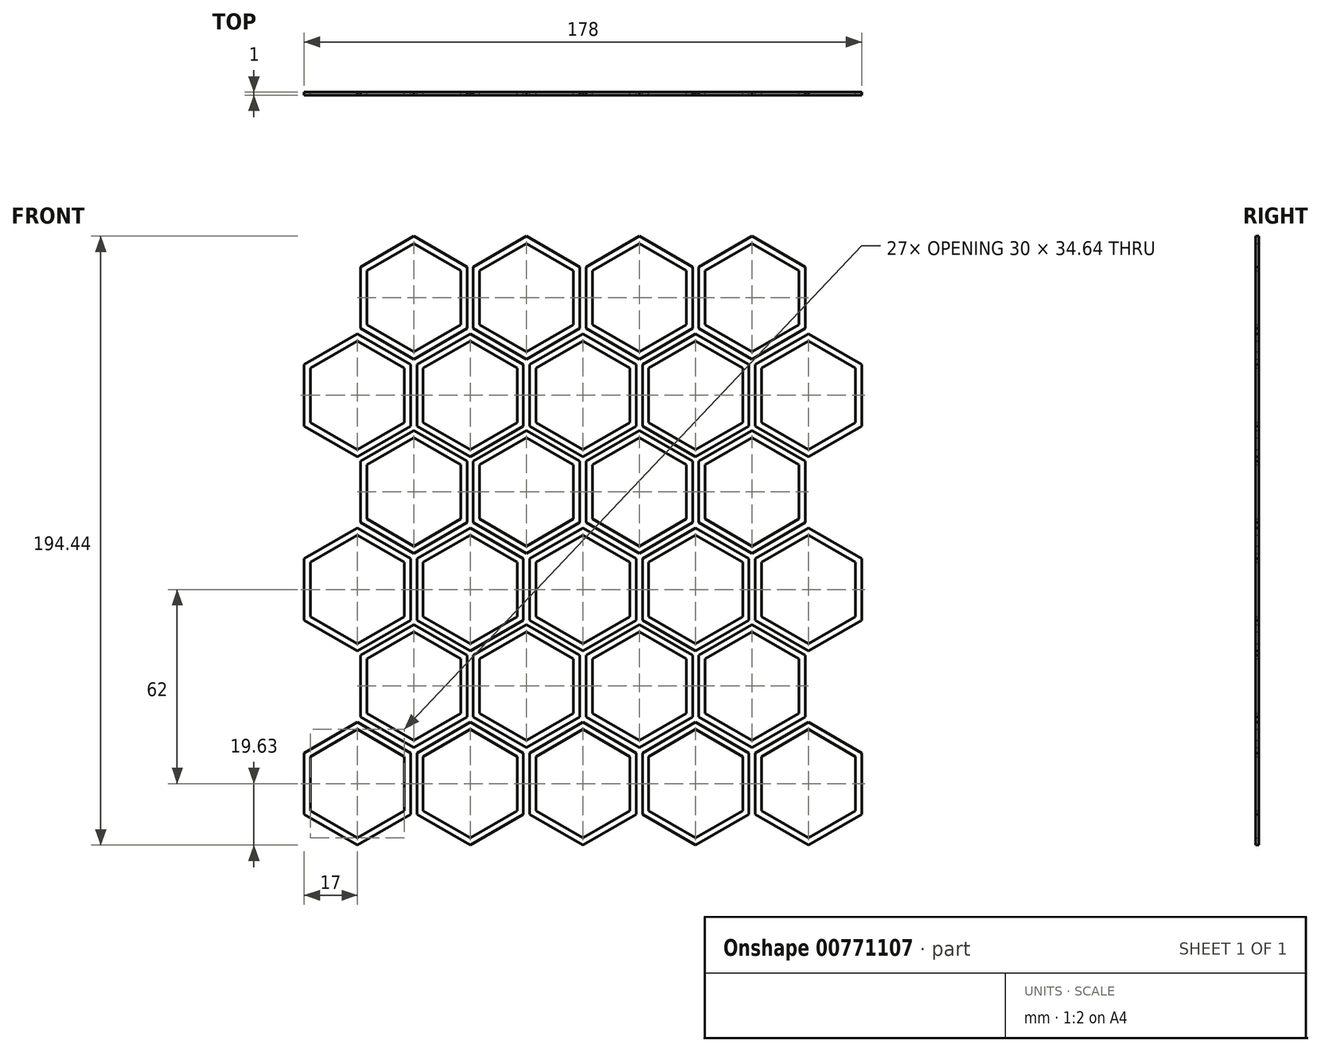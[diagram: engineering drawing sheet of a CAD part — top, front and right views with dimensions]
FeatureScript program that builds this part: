
annotation { "Feature Type Name" : "Feature", "Feature Type Description" : "" }
export const myFeature = defineFeature(function(context is Context, id is Id, definition is map)
    precondition{}
    {
        {
            var Q0;
            Q0=qCreatedBy(makeId("Front.planeOp"),FACE);
            var sketch = newSketch(context, id + "F0", { "sketchPlane" : qUnion([Q0])});
            skCircle(sketch, "E0.cCircle", {"center": v(0, 0) * mm, "radius": 15 * mm, "construction": true});
            skLineSegment(sketch, "E0.0", {"start": v(15, 8.66) * mm, "end": v(15, -8.66) * mm});
            skLineSegment(sketch, "E0.1", {"start": v(15, -8.66) * mm, "end": v(0, -17.32) * mm});
            skLineSegment(sketch, "E0.2", {"start": v(0, -17.32) * mm, "end": v(-15, -8.66) * mm});
            skLineSegment(sketch, "E0.3", {"start": v(-15, -8.66) * mm, "end": v(-15, 8.66) * mm});
            skLineSegment(sketch, "E0.4", {"start": v(-15, 8.66) * mm, "end": v(0, 17.32) * mm});
            skLineSegment(sketch, "E0.5", {"start": v(0, 17.32) * mm, "end": v(15, 8.66) * mm});
            skPoint(sketch, "E0.0.midPoint", {"position": v(15, 0) * mm});
            skLineSegment(sketch, "E1.0", {"start": v(0, 19.63) * mm, "end": v(17, 9.81) * mm});
            skLineSegment(sketch, "E1.1", {"start": v(17, -9.81) * mm, "end": v(0, -19.63) * mm});
            skLineSegment(sketch, "E1.2", {"start": v(0, -19.63) * mm, "end": v(-17, -9.81) * mm});
            skLineSegment(sketch, "E1.3", {"start": v(17, 9.81) * mm, "end": v(17, -9.81) * mm});
            skLineSegment(sketch, "E1.4", {"start": v(-17, -9.81) * mm, "end": v(-17, 9.81) * mm});
            skLineSegment(sketch, "E1.5", {"start": v(-17, 9.81) * mm, "end": v(0, 19.63) * mm});
            skLineSegment(sketch, "E2.1.0.0", {"start": v(36, 17.32) * mm, "end": v(51, 8.66) * mm});
            skLineSegment(sketch, "E2.1.0.1", {"start": v(36, 19.63) * mm, "end": v(53, 9.81) * mm});
            skLineSegment(sketch, "E2.1.0.2", {"start": v(53, -9.81) * mm, "end": v(36, -19.63) * mm});
            skLineSegment(sketch, "E2.1.0.3", {"start": v(36, -19.63) * mm, "end": v(19, -9.81) * mm});
            skLineSegment(sketch, "E2.1.0.4", {"start": v(53, 9.81) * mm, "end": v(53, -9.81) * mm});
            skLineSegment(sketch, "E2.1.0.5", {"start": v(19, -9.81) * mm, "end": v(19, 9.81) * mm});
            skLineSegment(sketch, "E2.1.0.6", {"start": v(19, 9.81) * mm, "end": v(36, 19.63) * mm});
            skPoint(sketch, "E2.1.0.7", {"position": v(51, 0) * mm});
            skLineSegment(sketch, "E2.1.0.8", {"start": v(21, 8.66) * mm, "end": v(36, 17.32) * mm});
            skLineSegment(sketch, "E2.1.0.9", {"start": v(21, -8.66) * mm, "end": v(21, 8.66) * mm});
            skLineSegment(sketch, "E2.1.0.10", {"start": v(36, -17.32) * mm, "end": v(21, -8.66) * mm});
            skLineSegment(sketch, "E2.1.0.11", {"start": v(51, -8.66) * mm, "end": v(36, -17.32) * mm});
            skLineSegment(sketch, "E2.1.0.12", {"start": v(51, 8.66) * mm, "end": v(51, -8.66) * mm});
            skCircle(sketch, "E2.1.0.13", {"center": v(36, 0) * mm, "radius": 15 * mm, "construction": true});
            skLineSegment(sketch, "E2.2.0.0", {"start": v(72, 17.32) * mm, "end": v(87, 8.66) * mm});
            skLineSegment(sketch, "E2.2.0.1", {"start": v(72, 19.63) * mm, "end": v(89, 9.81) * mm});
            skLineSegment(sketch, "E2.2.0.2", {"start": v(89, -9.81) * mm, "end": v(72, -19.63) * mm});
            skLineSegment(sketch, "E2.2.0.3", {"start": v(72, -19.63) * mm, "end": v(55, -9.81) * mm});
            skLineSegment(sketch, "E2.2.0.4", {"start": v(89, 9.81) * mm, "end": v(89, -9.81) * mm});
            skLineSegment(sketch, "E2.2.0.5", {"start": v(55, -9.81) * mm, "end": v(55, 9.81) * mm});
            skLineSegment(sketch, "E2.2.0.6", {"start": v(55, 9.81) * mm, "end": v(72, 19.63) * mm});
            skPoint(sketch, "E2.2.0.7", {"position": v(87, 0) * mm});
            skLineSegment(sketch, "E2.2.0.8", {"start": v(57, 8.66) * mm, "end": v(72, 17.32) * mm});
            skLineSegment(sketch, "E2.2.0.9", {"start": v(57, -8.66) * mm, "end": v(57, 8.66) * mm});
            skLineSegment(sketch, "E2.2.0.10", {"start": v(72, -17.32) * mm, "end": v(57, -8.66) * mm});
            skLineSegment(sketch, "E2.2.0.11", {"start": v(87, -8.66) * mm, "end": v(72, -17.32) * mm});
            skLineSegment(sketch, "E2.2.0.12", {"start": v(87, 8.66) * mm, "end": v(87, -8.66) * mm});
            skCircle(sketch, "E2.2.0.13", {"center": v(72, 0) * mm, "radius": 15 * mm, "construction": true});
            skLineSegment(sketch, "E2.direction1", {"start": v(-17, -9.81) * mm, "end": v(19, -9.81) * mm, "construction": true});
            skLineSegment(sketch, "E3", {"start": v(18, 6.46) * mm, "end": v(18, 61.1) * mm, "construction": true});
            skCircle(sketch, "E4.cCircle", {"center": v(18, 31.18) * mm, "radius": 15 * mm, "construction": true});
            skLineSegment(sketch, "E4.0", {"start": v(33, 39.84) * mm, "end": v(33, 22.52) * mm});
            skLineSegment(sketch, "E4.1", {"start": v(33, 22.52) * mm, "end": v(18, 13.86) * mm});
            skLineSegment(sketch, "E4.2", {"start": v(18, 13.86) * mm, "end": v(3, 22.52) * mm});
            skLineSegment(sketch, "E4.3", {"start": v(3, 22.52) * mm, "end": v(3, 39.84) * mm});
            skLineSegment(sketch, "E4.4", {"start": v(3, 39.84) * mm, "end": v(18, 48.5) * mm});
            skLineSegment(sketch, "E4.5", {"start": v(18, 48.5) * mm, "end": v(33, 39.84) * mm});
            skPoint(sketch, "E4.0.midPoint", {"position": v(33, 31.18) * mm});
            skLineSegment(sketch, "E5.1.0.0", {"start": v(54, 48.5) * mm, "end": v(69, 39.84) * mm});
            skLineSegment(sketch, "E5.1.0.1", {"start": v(39, 39.84) * mm, "end": v(54, 48.5) * mm});
            skLineSegment(sketch, "E5.1.0.2", {"start": v(39, 22.52) * mm, "end": v(39, 39.84) * mm});
            skLineSegment(sketch, "E5.1.0.3", {"start": v(54, 13.86) * mm, "end": v(39, 22.52) * mm});
            skLineSegment(sketch, "E5.1.0.4", {"start": v(69, 22.52) * mm, "end": v(54, 13.86) * mm});
            skLineSegment(sketch, "E5.1.0.5", {"start": v(69, 39.84) * mm, "end": v(69, 22.52) * mm});
            skLineSegment(sketch, "E5.direction1", {"start": v(3, 22.52) * mm, "end": v(39, 22.52) * mm, "construction": true});
            skLineSegment(sketch, "E6.0", {"start": v(35, 21.36) * mm, "end": v(18, 11.55) * mm});
            skLineSegment(sketch, "E6.1", {"start": v(1, 21.36) * mm, "end": v(1, 41) * mm});
            skLineSegment(sketch, "E6.2", {"start": v(1, 41) * mm, "end": v(18, 50.8) * mm});
            skLineSegment(sketch, "E6.3", {"start": v(18, 11.55) * mm, "end": v(1, 21.36) * mm});
            skLineSegment(sketch, "E6.4", {"start": v(18, 50.8) * mm, "end": v(35, 41) * mm});
            skLineSegment(sketch, "E6.5", {"start": v(35, 41) * mm, "end": v(35, 21.36) * mm});
            skLineSegment(sketch, "E7.0", {"start": v(37, 21.36) * mm, "end": v(37, 41) * mm});
            skLineSegment(sketch, "E7.1", {"start": v(54, 50.8) * mm, "end": v(71, 41) * mm});
            skLineSegment(sketch, "E7.2", {"start": v(71, 41) * mm, "end": v(71, 21.36) * mm});
            skLineSegment(sketch, "E7.3", {"start": v(37, 41) * mm, "end": v(54, 50.8) * mm});
            skLineSegment(sketch, "E7.4", {"start": v(71, 21.36) * mm, "end": v(54, 11.55) * mm});
            skLineSegment(sketch, "E7.5", {"start": v(54, 11.55) * mm, "end": v(37, 21.36) * mm});
            skLineSegment(sketch, "E8.0.3.0", {"start": v(108, 17.32) * mm, "end": v(123, 8.66) * mm});
            skLineSegment(sketch, "E8.3.3.0", {"start": v(108, 19.63) * mm, "end": v(125, 9.81) * mm});
            skLineSegment(sketch, "E8.6.3.0", {"start": v(125, -9.81) * mm, "end": v(108, -19.63) * mm});
            skLineSegment(sketch, "E8.9.3.0", {"start": v(108, -19.63) * mm, "end": v(91, -9.81) * mm});
            skLineSegment(sketch, "E8.12.3.0", {"start": v(125, 9.81) * mm, "end": v(125, -9.81) * mm});
            skLineSegment(sketch, "E8.15.3.0", {"start": v(91, -9.81) * mm, "end": v(91, 9.81) * mm});
            skLineSegment(sketch, "E8.18.3.0", {"start": v(91, 9.81) * mm, "end": v(108, 19.63) * mm});
            skPoint(sketch, "E8.21.3.0", {"position": v(123, 0) * mm});
            skLineSegment(sketch, "E8.22.3.0", {"start": v(93, 8.66) * mm, "end": v(108, 17.32) * mm});
            skLineSegment(sketch, "E8.25.3.0", {"start": v(93, -8.66) * mm, "end": v(93, 8.66) * mm});
            skLineSegment(sketch, "E8.28.3.0", {"start": v(108, -17.32) * mm, "end": v(93, -8.66) * mm});
            skLineSegment(sketch, "E8.31.3.0", {"start": v(123, -8.66) * mm, "end": v(108, -17.32) * mm});
            skLineSegment(sketch, "E8.34.3.0", {"start": v(123, 8.66) * mm, "end": v(123, -8.66) * mm});
            skCircle(sketch, "E8.37.3.0", {"center": v(108, 0) * mm, "radius": 15 * mm, "construction": true});
            skLineSegment(sketch, "E8.0.4.0", {"start": v(144, 17.32) * mm, "end": v(159, 8.66) * mm});
            skLineSegment(sketch, "E8.3.4.0", {"start": v(144, 19.63) * mm, "end": v(161, 9.81) * mm});
            skLineSegment(sketch, "E8.6.4.0", {"start": v(161, -9.81) * mm, "end": v(144, -19.63) * mm});
            skLineSegment(sketch, "E8.9.4.0", {"start": v(144, -19.63) * mm, "end": v(127, -9.81) * mm});
            skLineSegment(sketch, "E8.12.4.0", {"start": v(161, 9.81) * mm, "end": v(161, -9.81) * mm});
            skLineSegment(sketch, "E8.15.4.0", {"start": v(127, -9.81) * mm, "end": v(127, 9.81) * mm});
            skLineSegment(sketch, "E8.18.4.0", {"start": v(127, 9.81) * mm, "end": v(144, 19.63) * mm});
            skPoint(sketch, "E8.21.4.0", {"position": v(159, 0) * mm});
            skLineSegment(sketch, "E8.22.4.0", {"start": v(129, 8.66) * mm, "end": v(144, 17.32) * mm});
            skLineSegment(sketch, "E8.25.4.0", {"start": v(129, -8.66) * mm, "end": v(129, 8.66) * mm});
            skLineSegment(sketch, "E8.28.4.0", {"start": v(144, -17.32) * mm, "end": v(129, -8.66) * mm});
            skLineSegment(sketch, "E8.31.4.0", {"start": v(159, -8.66) * mm, "end": v(144, -17.32) * mm});
            skLineSegment(sketch, "E8.34.4.0", {"start": v(159, 8.66) * mm, "end": v(159, -8.66) * mm});
            skCircle(sketch, "E8.37.4.0", {"center": v(144, 0) * mm, "radius": 15 * mm, "construction": true});
            skLineSegment(sketch, "E9.0.2.0", {"start": v(90, 48.5) * mm, "end": v(105, 39.84) * mm});
            skLineSegment(sketch, "E9.3.2.0", {"start": v(75, 39.84) * mm, "end": v(90, 48.5) * mm});
            skLineSegment(sketch, "E9.6.2.0", {"start": v(75, 22.52) * mm, "end": v(75, 39.84) * mm});
            skLineSegment(sketch, "E9.9.2.0", {"start": v(90, 13.86) * mm, "end": v(75, 22.52) * mm});
            skLineSegment(sketch, "E9.12.2.0", {"start": v(105, 22.52) * mm, "end": v(90, 13.86) * mm});
            skLineSegment(sketch, "E9.15.2.0", {"start": v(105, 39.84) * mm, "end": v(105, 22.52) * mm});
            skLineSegment(sketch, "E10.1.0.0", {"start": v(107, 41) * mm, "end": v(107, 21.36) * mm});
            skLineSegment(sketch, "E10.1.0.1", {"start": v(90, 50.8) * mm, "end": v(107, 41) * mm});
            skLineSegment(sketch, "E10.1.0.2", {"start": v(73, 41) * mm, "end": v(90, 50.8) * mm});
            skLineSegment(sketch, "E10.1.0.3", {"start": v(73, 21.36) * mm, "end": v(73, 41) * mm});
            skLineSegment(sketch, "E10.1.0.4", {"start": v(90, 11.55) * mm, "end": v(73, 21.36) * mm});
            skLineSegment(sketch, "E10.1.0.11", {"start": v(107, 21.36) * mm, "end": v(90, 11.55) * mm});
            skLineSegment(sketch, "E10.2.0.0", {"start": v(143, 41) * mm, "end": v(143, 21.36) * mm});
            skLineSegment(sketch, "E10.2.0.1", {"start": v(126, 50.8) * mm, "end": v(143, 41) * mm});
            skLineSegment(sketch, "E10.2.0.2", {"start": v(109, 41) * mm, "end": v(126, 50.8) * mm});
            skLineSegment(sketch, "E10.2.0.3", {"start": v(109, 21.36) * mm, "end": v(109, 41) * mm});
            skLineSegment(sketch, "E10.2.0.4", {"start": v(126, 11.55) * mm, "end": v(109, 21.36) * mm});
            skLineSegment(sketch, "E10.2.0.5", {"start": v(126, 13.86) * mm, "end": v(111, 22.52) * mm});
            skLineSegment(sketch, "E10.2.0.6", {"start": v(111, 39.84) * mm, "end": v(126, 48.5) * mm});
            skLineSegment(sketch, "E10.2.0.7", {"start": v(126, 48.5) * mm, "end": v(141, 39.84) * mm});
            skLineSegment(sketch, "E10.2.0.8", {"start": v(111, 22.52) * mm, "end": v(111, 39.84) * mm});
            skLineSegment(sketch, "E10.2.0.9", {"start": v(141, 22.52) * mm, "end": v(126, 13.86) * mm});
            skLineSegment(sketch, "E10.2.0.10", {"start": v(141, 39.84) * mm, "end": v(141, 22.52) * mm});
            skLineSegment(sketch, "E10.2.0.11", {"start": v(143, 21.36) * mm, "end": v(126, 11.55) * mm});
            skLineSegment(sketch, "E10.direction1", {"start": v(37, 21.36) * mm, "end": v(73, 21.36) * mm, "construction": true});
            skLineSegment(sketch, "E11.0.1.0", {"start": v(54, 112.8) * mm, "end": v(71, 103) * mm});
            skLineSegment(sketch, "E11.0.1.1", {"start": v(0, 79.32) * mm, "end": v(15, 70.66) * mm});
            skLineSegment(sketch, "E11.0.1.2", {"start": v(87, 70.66) * mm, "end": v(87, 53.34) * mm});
            skLineSegment(sketch, "E11.0.1.3", {"start": v(0, 81.63) * mm, "end": v(17, 71.81) * mm});
            skLineSegment(sketch, "E11.0.1.4", {"start": v(17, 52.19) * mm, "end": v(0, 42.37) * mm});
            skLineSegment(sketch, "E11.0.1.5", {"start": v(0, 42.37) * mm, "end": v(-17, 52.19) * mm});
            skLineSegment(sketch, "E11.0.1.6", {"start": v(17, 71.81) * mm, "end": v(17, 52.19) * mm});
            skLineSegment(sketch, "E11.0.1.7", {"start": v(-17, 52.19) * mm, "end": v(-17, 71.81) * mm});
            skLineSegment(sketch, "E11.0.1.8", {"start": v(-17, 71.81) * mm, "end": v(0, 81.63) * mm});
            skLineSegment(sketch, "E11.0.1.9", {"start": v(126, 112.8) * mm, "end": v(143, 103) * mm});
            skLineSegment(sketch, "E11.0.1.10", {"start": v(3, 101.84) * mm, "end": v(18, 110.5) * mm});
            skLineSegment(sketch, "E11.0.1.11", {"start": v(89, 71.81) * mm, "end": v(89, 52.19) * mm});
            skLineSegment(sketch, "E11.0.1.12", {"start": v(35, 83.36) * mm, "end": v(18, 73.55) * mm});
            skLineSegment(sketch, "E11.0.1.13", {"start": v(51, 53.34) * mm, "end": v(36, 44.68) * mm});
            skLineSegment(sketch, "E11.0.1.14", {"start": v(69, 101.84) * mm, "end": v(69, 84.52) * mm});
            skLineSegment(sketch, "E11.0.1.15", {"start": v(18, 75.86) * mm, "end": v(3, 84.52) * mm});
            skLineSegment(sketch, "E11.0.1.16", {"start": v(-17, 52.19) * mm, "end": v(19, 52.19) * mm, "construction": true});
            skLineSegment(sketch, "E11.0.1.17", {"start": v(111, 84.52) * mm, "end": v(111, 101.84) * mm});
            skLineSegment(sketch, "E11.0.1.18", {"start": v(90, 73.55) * mm, "end": v(73, 83.36) * mm});
            skLineSegment(sketch, "E11.0.1.19", {"start": v(129, 70.66) * mm, "end": v(144, 79.32) * mm});
            skLineSegment(sketch, "E11.0.1.20", {"start": v(125, 71.81) * mm, "end": v(125, 52.19) * mm});
            skPoint(sketch, "E11.0.1.21", {"position": v(159, 62) * mm});
            skLineSegment(sketch, "E11.0.1.22", {"start": v(36, 44.68) * mm, "end": v(21, 53.34) * mm});
            skPoint(sketch, "E11.0.1.23", {"position": v(87, 62) * mm});
            skCircle(sketch, "E11.0.1.24", {"center": v(108, 62) * mm, "radius": 15 * mm, "construction": true});
            skLineSegment(sketch, "E11.0.1.25", {"start": v(107, 83.36) * mm, "end": v(90, 73.55) * mm});
            skLineSegment(sketch, "E11.0.1.26", {"start": v(90, 112.8) * mm, "end": v(107, 103) * mm});
            skLineSegment(sketch, "E11.0.1.27", {"start": v(127, 71.81) * mm, "end": v(144, 81.63) * mm});
            skLineSegment(sketch, "E11.0.1.28", {"start": v(71, 103) * mm, "end": v(71, 83.36) * mm});
            skLineSegment(sketch, "E11.0.1.29", {"start": v(108, 42.37) * mm, "end": v(91, 52.19) * mm});
            skLineSegment(sketch, "E11.0.1.30", {"start": v(18, 110.5) * mm, "end": v(33, 101.84) * mm});
            skLineSegment(sketch, "E11.0.1.31", {"start": v(55, 52.19) * mm, "end": v(55, 71.81) * mm});
            skLineSegment(sketch, "E11.0.1.32", {"start": v(3, 84.52) * mm, "end": v(39, 84.52) * mm, "construction": true});
            skLineSegment(sketch, "E11.0.1.33", {"start": v(126, 110.5) * mm, "end": v(141, 101.84) * mm});
            skLineSegment(sketch, "E11.0.1.34", {"start": v(35, 103) * mm, "end": v(35, 83.36) * mm});
            skCircle(sketch, "E11.0.1.35", {"center": v(72, 62) * mm, "radius": 15 * mm, "construction": true});
            skLineSegment(sketch, "E11.0.1.36", {"start": v(75, 84.52) * mm, "end": v(75, 101.84) * mm});
            skLineSegment(sketch, "E11.0.1.37", {"start": v(143, 103) * mm, "end": v(143, 83.36) * mm});
            skLineSegment(sketch, "E11.0.1.38", {"start": v(73, 83.36) * mm, "end": v(73, 103) * mm});
            skLineSegment(sketch, "E11.0.1.39", {"start": v(36, 42.37) * mm, "end": v(19, 52.19) * mm});
            skLineSegment(sketch, "E11.0.1.40", {"start": v(144, 79.32) * mm, "end": v(159, 70.66) * mm});
            skLineSegment(sketch, "E11.0.1.41", {"start": v(37, 103) * mm, "end": v(54, 112.8) * mm});
            skLineSegment(sketch, "E11.0.1.42", {"start": v(36, 79.32) * mm, "end": v(51, 70.66) * mm});
            skLineSegment(sketch, "E11.0.1.43", {"start": v(36, 81.63) * mm, "end": v(53, 71.81) * mm});
            skLineSegment(sketch, "E11.0.1.44", {"start": v(53, 52.19) * mm, "end": v(36, 42.37) * mm});
            skCircle(sketch, "E11.0.1.45", {"center": v(0, 62) * mm, "radius": 15 * mm, "construction": true});
            skLineSegment(sketch, "E11.0.1.46", {"start": v(15, 70.66) * mm, "end": v(15, 53.34) * mm});
            skLineSegment(sketch, "E11.0.1.47", {"start": v(54, 110.5) * mm, "end": v(69, 101.84) * mm});
            skLineSegment(sketch, "E11.0.1.48", {"start": v(111, 101.84) * mm, "end": v(126, 110.5) * mm});
            skLineSegment(sketch, "E11.0.1.49", {"start": v(55, 71.81) * mm, "end": v(72, 81.63) * mm});
            skLineSegment(sketch, "E11.0.1.50", {"start": v(15, 53.34) * mm, "end": v(0, 44.68) * mm});
            skLineSegment(sketch, "E11.0.1.51", {"start": v(0, 44.68) * mm, "end": v(-15, 53.34) * mm});
            skLineSegment(sketch, "E11.0.1.52", {"start": v(125, 52.19) * mm, "end": v(108, 42.37) * mm});
            skLineSegment(sketch, "E11.0.1.53", {"start": v(123, 70.66) * mm, "end": v(123, 53.34) * mm});
            skLineSegment(sketch, "E11.0.1.54", {"start": v(127, 52.19) * mm, "end": v(127, 71.81) * mm});
            skLineSegment(sketch, "E11.0.1.55", {"start": v(21, 53.34) * mm, "end": v(21, 70.66) * mm});
            skLineSegment(sketch, "E11.0.1.56", {"start": v(108, 44.68) * mm, "end": v(93, 53.34) * mm});
            skCircle(sketch, "E11.0.1.57", {"center": v(144, 62) * mm, "radius": 15 * mm, "construction": true});
            skLineSegment(sketch, "E11.0.1.58", {"start": v(73, 103) * mm, "end": v(90, 112.8) * mm});
            skLineSegment(sketch, "E11.0.1.59", {"start": v(-15, 70.66) * mm, "end": v(0, 79.32) * mm});
            skLineSegment(sketch, "E11.0.1.60", {"start": v(-15, 53.34) * mm, "end": v(-15, 70.66) * mm});
            skLineSegment(sketch, "E11.0.1.61", {"start": v(89, 52.19) * mm, "end": v(72, 42.37) * mm});
            skPoint(sketch, "E11.0.1.62", {"position": v(51, 62) * mm});
            skPoint(sketch, "E11.0.1.63", {"position": v(15, 62) * mm});
            skPoint(sketch, "E11.0.1.64", {"position": v(123, 62) * mm});
            skCircle(sketch, "E11.0.1.65", {"center": v(18, 93.18) * mm, "radius": 15 * mm, "construction": true});
            skLineSegment(sketch, "E11.0.1.66", {"start": v(126, 73.55) * mm, "end": v(109, 83.36) * mm});
            skLineSegment(sketch, "E11.0.1.67", {"start": v(18, 68.46) * mm, "end": v(18, 123.1) * mm, "construction": true});
            skLineSegment(sketch, "E11.0.1.68", {"start": v(51, 70.66) * mm, "end": v(51, 53.34) * mm});
            skLineSegment(sketch, "E11.0.1.69", {"start": v(1, 103) * mm, "end": v(18, 112.8) * mm});
            skLineSegment(sketch, "E11.0.1.70", {"start": v(71, 83.36) * mm, "end": v(54, 73.55) * mm});
            skLineSegment(sketch, "E11.0.1.71", {"start": v(33, 101.84) * mm, "end": v(33, 84.52) * mm});
            skLineSegment(sketch, "E11.0.1.72", {"start": v(39, 101.84) * mm, "end": v(54, 110.5) * mm});
            skLineSegment(sketch, "E11.0.1.73", {"start": v(90, 75.86) * mm, "end": v(75, 84.52) * mm});
            skLineSegment(sketch, "E11.0.1.74", {"start": v(72, 42.37) * mm, "end": v(55, 52.19) * mm});
            skLineSegment(sketch, "E11.0.1.75", {"start": v(159, 70.66) * mm, "end": v(159, 53.34) * mm});
            skLineSegment(sketch, "E11.0.1.76", {"start": v(19, 52.19) * mm, "end": v(19, 71.81) * mm});
            skLineSegment(sketch, "E11.0.1.77", {"start": v(108, 79.32) * mm, "end": v(123, 70.66) * mm});
            skLineSegment(sketch, "E11.0.1.78", {"start": v(109, 103) * mm, "end": v(126, 112.8) * mm});
            skLineSegment(sketch, "E11.0.1.79", {"start": v(143, 83.36) * mm, "end": v(126, 73.55) * mm});
            skLineSegment(sketch, "E11.0.1.80", {"start": v(3, 84.52) * mm, "end": v(3, 101.84) * mm});
            skLineSegment(sketch, "E11.0.1.81", {"start": v(69, 84.52) * mm, "end": v(54, 75.86) * mm});
            skLineSegment(sketch, "E11.0.1.82", {"start": v(18, 112.8) * mm, "end": v(35, 103) * mm});
            skLineSegment(sketch, "E11.0.1.83", {"start": v(161, 71.81) * mm, "end": v(161, 52.19) * mm});
            skLineSegment(sketch, "E11.0.1.84", {"start": v(105, 101.84) * mm, "end": v(105, 84.52) * mm});
            skCircle(sketch, "E11.0.1.85", {"center": v(36, 62) * mm, "radius": 15 * mm, "construction": true});
            skLineSegment(sketch, "E11.0.1.86", {"start": v(129, 53.34) * mm, "end": v(129, 70.66) * mm});
            skLineSegment(sketch, "E11.0.1.87", {"start": v(159, 53.34) * mm, "end": v(144, 44.68) * mm});
            skLineSegment(sketch, "E11.0.1.88", {"start": v(90, 110.5) * mm, "end": v(105, 101.84) * mm});
            skLineSegment(sketch, "E11.0.1.89", {"start": v(126, 75.86) * mm, "end": v(111, 84.52) * mm});
            skLineSegment(sketch, "E11.0.1.90", {"start": v(33, 84.52) * mm, "end": v(18, 75.86) * mm});
            skLineSegment(sketch, "E11.0.1.91", {"start": v(91, 52.19) * mm, "end": v(91, 71.81) * mm});
            skLineSegment(sketch, "E11.0.1.92", {"start": v(93, 70.66) * mm, "end": v(108, 79.32) * mm});
            skLineSegment(sketch, "E11.0.1.93", {"start": v(144, 81.63) * mm, "end": v(161, 71.81) * mm});
            skLineSegment(sketch, "E11.0.1.94", {"start": v(18, 73.55) * mm, "end": v(1, 83.36) * mm});
            skLineSegment(sketch, "E11.0.1.95", {"start": v(93, 53.34) * mm, "end": v(93, 70.66) * mm});
            skLineSegment(sketch, "E11.0.1.96", {"start": v(123, 53.34) * mm, "end": v(108, 44.68) * mm});
            skLineSegment(sketch, "E11.0.1.97", {"start": v(75, 101.84) * mm, "end": v(90, 110.5) * mm});
            skLineSegment(sketch, "E11.0.1.98", {"start": v(39, 84.52) * mm, "end": v(39, 101.84) * mm});
            skLineSegment(sketch, "E11.0.1.99", {"start": v(57, 53.34) * mm, "end": v(57, 70.66) * mm});
            skLineSegment(sketch, "E11.0.1.100", {"start": v(144, 44.68) * mm, "end": v(129, 53.34) * mm});
            skLineSegment(sketch, "E11.0.1.101", {"start": v(141, 101.84) * mm, "end": v(141, 84.52) * mm});
            skLineSegment(sketch, "E11.0.1.102", {"start": v(54, 75.86) * mm, "end": v(39, 84.52) * mm});
            skLineSegment(sketch, "E11.0.1.103", {"start": v(141, 84.52) * mm, "end": v(126, 75.86) * mm});
            skLineSegment(sketch, "E11.0.1.104", {"start": v(87, 53.34) * mm, "end": v(72, 44.68) * mm});
            skLineSegment(sketch, "E11.0.1.105", {"start": v(91, 71.81) * mm, "end": v(108, 81.63) * mm});
            skLineSegment(sketch, "E11.0.1.106", {"start": v(53, 71.81) * mm, "end": v(53, 52.19) * mm});
            skLineSegment(sketch, "E11.0.1.107", {"start": v(72, 44.68) * mm, "end": v(57, 53.34) * mm});
            skLineSegment(sketch, "E11.0.1.108", {"start": v(72, 81.63) * mm, "end": v(89, 71.81) * mm});
            skLineSegment(sketch, "E11.0.1.109", {"start": v(109, 83.36) * mm, "end": v(109, 103) * mm});
            skLineSegment(sketch, "E11.0.1.110", {"start": v(161, 52.19) * mm, "end": v(144, 42.37) * mm});
            skLineSegment(sketch, "E11.0.1.111", {"start": v(19, 71.81) * mm, "end": v(36, 81.63) * mm});
            skLineSegment(sketch, "E11.0.1.112", {"start": v(107, 103) * mm, "end": v(107, 83.36) * mm});
            skLineSegment(sketch, "E11.0.1.113", {"start": v(57, 70.66) * mm, "end": v(72, 79.32) * mm});
            skLineSegment(sketch, "E11.0.1.114", {"start": v(1, 83.36) * mm, "end": v(1, 103) * mm});
            skPoint(sketch, "E11.0.1.115", {"position": v(33, 93.18) * mm});
            skLineSegment(sketch, "E11.0.1.116", {"start": v(108, 81.63) * mm, "end": v(125, 71.81) * mm});
            skLineSegment(sketch, "E11.0.1.117", {"start": v(37, 83.36) * mm, "end": v(73, 83.36) * mm, "construction": true});
            skLineSegment(sketch, "E11.0.1.118", {"start": v(54, 73.55) * mm, "end": v(37, 83.36) * mm});
            skLineSegment(sketch, "E11.0.1.119", {"start": v(144, 42.37) * mm, "end": v(127, 52.19) * mm});
            skLineSegment(sketch, "E11.0.1.120", {"start": v(105, 84.52) * mm, "end": v(90, 75.86) * mm});
            skLineSegment(sketch, "E11.0.1.121", {"start": v(72, 79.32) * mm, "end": v(87, 70.66) * mm});
            skLineSegment(sketch, "E11.0.1.122", {"start": v(37, 83.36) * mm, "end": v(37, 103) * mm});
            skLineSegment(sketch, "E11.0.1.123", {"start": v(21, 70.66) * mm, "end": v(36, 79.32) * mm});
            skLineSegment(sketch, "E11.0.1.124", {"start": v(90, 75.86) * mm, "end": v(75, 84.52) * mm});
            skLineSegment(sketch, "E11.0.1.125", {"start": v(105, 84.52) * mm, "end": v(90, 75.86) * mm});
            skLineSegment(sketch, "E11.0.1.126", {"start": v(75, 101.84) * mm, "end": v(90, 110.5) * mm});
            skLineSegment(sketch, "E11.0.1.127", {"start": v(105, 101.84) * mm, "end": v(105, 84.52) * mm});
            skLineSegment(sketch, "E11.0.1.128", {"start": v(90, 110.5) * mm, "end": v(105, 101.84) * mm});
            skLineSegment(sketch, "E11.0.1.129", {"start": v(75, 84.52) * mm, "end": v(75, 101.84) * mm});
            skLineSegment(sketch, "E11.0.2.0", {"start": v(54, 174.8) * mm, "end": v(71, 165) * mm});
            skLineSegment(sketch, "E11.0.2.1", {"start": v(0, 141.32) * mm, "end": v(15, 132.66) * mm});
            skLineSegment(sketch, "E11.0.2.2", {"start": v(87, 132.66) * mm, "end": v(87, 115.34) * mm});
            skLineSegment(sketch, "E11.0.2.3", {"start": v(0, 143.63) * mm, "end": v(17, 133.81) * mm});
            skLineSegment(sketch, "E11.0.2.4", {"start": v(17, 114.19) * mm, "end": v(0, 104.37) * mm});
            skLineSegment(sketch, "E11.0.2.5", {"start": v(0, 104.37) * mm, "end": v(-17, 114.19) * mm});
            skLineSegment(sketch, "E11.0.2.6", {"start": v(17, 133.81) * mm, "end": v(17, 114.19) * mm});
            skLineSegment(sketch, "E11.0.2.7", {"start": v(-17, 114.19) * mm, "end": v(-17, 133.81) * mm});
            skLineSegment(sketch, "E11.0.2.8", {"start": v(-17, 133.81) * mm, "end": v(0, 143.63) * mm});
            skLineSegment(sketch, "E11.0.2.9", {"start": v(126, 174.8) * mm, "end": v(143, 165) * mm});
            skLineSegment(sketch, "E11.0.2.10", {"start": v(3, 163.84) * mm, "end": v(18, 172.5) * mm});
            skLineSegment(sketch, "E11.0.2.11", {"start": v(89, 133.81) * mm, "end": v(89, 114.19) * mm});
            skLineSegment(sketch, "E11.0.2.12", {"start": v(35, 145.36) * mm, "end": v(18, 135.55) * mm});
            skLineSegment(sketch, "E11.0.2.13", {"start": v(51, 115.34) * mm, "end": v(36, 106.68) * mm});
            skLineSegment(sketch, "E11.0.2.14", {"start": v(69, 163.84) * mm, "end": v(69, 146.52) * mm});
            skLineSegment(sketch, "E11.0.2.15", {"start": v(18, 137.86) * mm, "end": v(3, 146.52) * mm});
            skLineSegment(sketch, "E11.0.2.16", {"start": v(-17, 114.19) * mm, "end": v(19, 114.19) * mm, "construction": true});
            skLineSegment(sketch, "E11.0.2.17", {"start": v(111, 146.52) * mm, "end": v(111, 163.84) * mm});
            skLineSegment(sketch, "E11.0.2.18", {"start": v(90, 135.55) * mm, "end": v(73, 145.36) * mm});
            skLineSegment(sketch, "E11.0.2.19", {"start": v(129, 132.66) * mm, "end": v(144, 141.32) * mm});
            skLineSegment(sketch, "E11.0.2.20", {"start": v(125, 133.81) * mm, "end": v(125, 114.19) * mm});
            skPoint(sketch, "E11.0.2.21", {"position": v(159, 124) * mm});
            skLineSegment(sketch, "E11.0.2.22", {"start": v(36, 106.68) * mm, "end": v(21, 115.34) * mm});
            skPoint(sketch, "E11.0.2.23", {"position": v(87, 124) * mm});
            skCircle(sketch, "E11.0.2.24", {"center": v(108, 124) * mm, "radius": 15 * mm, "construction": true});
            skLineSegment(sketch, "E11.0.2.25", {"start": v(107, 145.36) * mm, "end": v(90, 135.55) * mm});
            skLineSegment(sketch, "E11.0.2.26", {"start": v(90, 174.8) * mm, "end": v(107, 165) * mm});
            skLineSegment(sketch, "E11.0.2.27", {"start": v(127, 133.81) * mm, "end": v(144, 143.63) * mm});
            skLineSegment(sketch, "E11.0.2.28", {"start": v(71, 165) * mm, "end": v(71, 145.36) * mm});
            skLineSegment(sketch, "E11.0.2.29", {"start": v(108, 104.37) * mm, "end": v(91, 114.19) * mm});
            skLineSegment(sketch, "E11.0.2.30", {"start": v(18, 172.5) * mm, "end": v(33, 163.84) * mm});
            skLineSegment(sketch, "E11.0.2.31", {"start": v(55, 114.19) * mm, "end": v(55, 133.81) * mm});
            skLineSegment(sketch, "E11.0.2.32", {"start": v(3, 146.52) * mm, "end": v(39, 146.52) * mm, "construction": true});
            skLineSegment(sketch, "E11.0.2.33", {"start": v(126, 172.5) * mm, "end": v(141, 163.84) * mm});
            skLineSegment(sketch, "E11.0.2.34", {"start": v(35, 165) * mm, "end": v(35, 145.36) * mm});
            skCircle(sketch, "E11.0.2.35", {"center": v(72, 124) * mm, "radius": 15 * mm, "construction": true});
            skLineSegment(sketch, "E11.0.2.36", {"start": v(75, 146.52) * mm, "end": v(75, 163.84) * mm});
            skLineSegment(sketch, "E11.0.2.37", {"start": v(143, 165) * mm, "end": v(143, 145.36) * mm});
            skLineSegment(sketch, "E11.0.2.38", {"start": v(73, 145.36) * mm, "end": v(73, 165) * mm});
            skLineSegment(sketch, "E11.0.2.39", {"start": v(36, 104.37) * mm, "end": v(19, 114.19) * mm});
            skLineSegment(sketch, "E11.0.2.40", {"start": v(144, 141.32) * mm, "end": v(159, 132.66) * mm});
            skLineSegment(sketch, "E11.0.2.41", {"start": v(37, 165) * mm, "end": v(54, 174.8) * mm});
            skLineSegment(sketch, "E11.0.2.42", {"start": v(36, 141.32) * mm, "end": v(51, 132.66) * mm});
            skLineSegment(sketch, "E11.0.2.43", {"start": v(36, 143.63) * mm, "end": v(53, 133.81) * mm});
            skLineSegment(sketch, "E11.0.2.44", {"start": v(53, 114.19) * mm, "end": v(36, 104.37) * mm});
            skCircle(sketch, "E11.0.2.45", {"center": v(0, 124) * mm, "radius": 15 * mm, "construction": true});
            skLineSegment(sketch, "E11.0.2.46", {"start": v(15, 132.66) * mm, "end": v(15, 115.34) * mm});
            skLineSegment(sketch, "E11.0.2.47", {"start": v(54, 172.5) * mm, "end": v(69, 163.84) * mm});
            skLineSegment(sketch, "E11.0.2.48", {"start": v(111, 163.84) * mm, "end": v(126, 172.5) * mm});
            skLineSegment(sketch, "E11.0.2.49", {"start": v(55, 133.81) * mm, "end": v(72, 143.63) * mm});
            skLineSegment(sketch, "E11.0.2.50", {"start": v(15, 115.34) * mm, "end": v(0, 106.68) * mm});
            skLineSegment(sketch, "E11.0.2.51", {"start": v(0, 106.68) * mm, "end": v(-15, 115.34) * mm});
            skLineSegment(sketch, "E11.0.2.52", {"start": v(125, 114.19) * mm, "end": v(108, 104.37) * mm});
            skLineSegment(sketch, "E11.0.2.53", {"start": v(123, 132.66) * mm, "end": v(123, 115.34) * mm});
            skLineSegment(sketch, "E11.0.2.54", {"start": v(127, 114.19) * mm, "end": v(127, 133.81) * mm});
            skLineSegment(sketch, "E11.0.2.55", {"start": v(21, 115.34) * mm, "end": v(21, 132.66) * mm});
            skLineSegment(sketch, "E11.0.2.56", {"start": v(108, 106.68) * mm, "end": v(93, 115.34) * mm});
            skCircle(sketch, "E11.0.2.57", {"center": v(144, 124) * mm, "radius": 15 * mm, "construction": true});
            skLineSegment(sketch, "E11.0.2.58", {"start": v(73, 165) * mm, "end": v(90, 174.8) * mm});
            skLineSegment(sketch, "E11.0.2.59", {"start": v(-15, 132.66) * mm, "end": v(0, 141.32) * mm});
            skLineSegment(sketch, "E11.0.2.60", {"start": v(-15, 115.34) * mm, "end": v(-15, 132.66) * mm});
            skLineSegment(sketch, "E11.0.2.61", {"start": v(89, 114.19) * mm, "end": v(72, 104.37) * mm});
            skPoint(sketch, "E11.0.2.62", {"position": v(51, 124) * mm});
            skPoint(sketch, "E11.0.2.63", {"position": v(15, 124) * mm});
            skPoint(sketch, "E11.0.2.64", {"position": v(123, 124) * mm});
            skCircle(sketch, "E11.0.2.65", {"center": v(18, 155.18) * mm, "radius": 15 * mm, "construction": true});
            skLineSegment(sketch, "E11.0.2.66", {"start": v(126, 135.55) * mm, "end": v(109, 145.36) * mm});
            skLineSegment(sketch, "E11.0.2.67", {"start": v(18, 130.46) * mm, "end": v(18, 185.1) * mm, "construction": true});
            skLineSegment(sketch, "E11.0.2.68", {"start": v(51, 132.66) * mm, "end": v(51, 115.34) * mm});
            skLineSegment(sketch, "E11.0.2.69", {"start": v(1, 165) * mm, "end": v(18, 174.8) * mm});
            skLineSegment(sketch, "E11.0.2.70", {"start": v(71, 145.36) * mm, "end": v(54, 135.55) * mm});
            skLineSegment(sketch, "E11.0.2.71", {"start": v(33, 163.84) * mm, "end": v(33, 146.52) * mm});
            skLineSegment(sketch, "E11.0.2.72", {"start": v(39, 163.84) * mm, "end": v(54, 172.5) * mm});
            skLineSegment(sketch, "E11.0.2.73", {"start": v(90, 137.86) * mm, "end": v(75, 146.52) * mm});
            skLineSegment(sketch, "E11.0.2.74", {"start": v(72, 104.37) * mm, "end": v(55, 114.19) * mm});
            skLineSegment(sketch, "E11.0.2.75", {"start": v(159, 132.66) * mm, "end": v(159, 115.34) * mm});
            skLineSegment(sketch, "E11.0.2.76", {"start": v(19, 114.19) * mm, "end": v(19, 133.81) * mm});
            skLineSegment(sketch, "E11.0.2.77", {"start": v(108, 141.32) * mm, "end": v(123, 132.66) * mm});
            skLineSegment(sketch, "E11.0.2.78", {"start": v(109, 165) * mm, "end": v(126, 174.8) * mm});
            skLineSegment(sketch, "E11.0.2.79", {"start": v(143, 145.36) * mm, "end": v(126, 135.55) * mm});
            skLineSegment(sketch, "E11.0.2.80", {"start": v(3, 146.52) * mm, "end": v(3, 163.84) * mm});
            skLineSegment(sketch, "E11.0.2.81", {"start": v(69, 146.52) * mm, "end": v(54, 137.86) * mm});
            skLineSegment(sketch, "E11.0.2.82", {"start": v(18, 174.8) * mm, "end": v(35, 165) * mm});
            skLineSegment(sketch, "E11.0.2.83", {"start": v(161, 133.81) * mm, "end": v(161, 114.19) * mm});
            skLineSegment(sketch, "E11.0.2.84", {"start": v(105, 163.84) * mm, "end": v(105, 146.52) * mm});
            skCircle(sketch, "E11.0.2.85", {"center": v(36, 124) * mm, "radius": 15 * mm, "construction": true});
            skLineSegment(sketch, "E11.0.2.86", {"start": v(129, 115.34) * mm, "end": v(129, 132.66) * mm});
            skLineSegment(sketch, "E11.0.2.87", {"start": v(159, 115.34) * mm, "end": v(144, 106.68) * mm});
            skLineSegment(sketch, "E11.0.2.88", {"start": v(90, 172.5) * mm, "end": v(105, 163.84) * mm});
            skLineSegment(sketch, "E11.0.2.89", {"start": v(126, 137.86) * mm, "end": v(111, 146.52) * mm});
            skLineSegment(sketch, "E11.0.2.90", {"start": v(33, 146.52) * mm, "end": v(18, 137.86) * mm});
            skLineSegment(sketch, "E11.0.2.91", {"start": v(91, 114.19) * mm, "end": v(91, 133.81) * mm});
            skLineSegment(sketch, "E11.0.2.92", {"start": v(93, 132.66) * mm, "end": v(108, 141.32) * mm});
            skLineSegment(sketch, "E11.0.2.93", {"start": v(144, 143.63) * mm, "end": v(161, 133.81) * mm});
            skLineSegment(sketch, "E11.0.2.94", {"start": v(18, 135.55) * mm, "end": v(1, 145.36) * mm});
            skLineSegment(sketch, "E11.0.2.95", {"start": v(93, 115.34) * mm, "end": v(93, 132.66) * mm});
            skLineSegment(sketch, "E11.0.2.96", {"start": v(123, 115.34) * mm, "end": v(108, 106.68) * mm});
            skLineSegment(sketch, "E11.0.2.97", {"start": v(75, 163.84) * mm, "end": v(90, 172.5) * mm});
            skLineSegment(sketch, "E11.0.2.98", {"start": v(39, 146.52) * mm, "end": v(39, 163.84) * mm});
            skLineSegment(sketch, "E11.0.2.99", {"start": v(57, 115.34) * mm, "end": v(57, 132.66) * mm});
            skLineSegment(sketch, "E11.0.2.100", {"start": v(144, 106.68) * mm, "end": v(129, 115.34) * mm});
            skLineSegment(sketch, "E11.0.2.101", {"start": v(141, 163.84) * mm, "end": v(141, 146.52) * mm});
            skLineSegment(sketch, "E11.0.2.102", {"start": v(54, 137.86) * mm, "end": v(39, 146.52) * mm});
            skLineSegment(sketch, "E11.0.2.103", {"start": v(141, 146.52) * mm, "end": v(126, 137.86) * mm});
            skLineSegment(sketch, "E11.0.2.104", {"start": v(87, 115.34) * mm, "end": v(72, 106.68) * mm});
            skLineSegment(sketch, "E11.0.2.105", {"start": v(91, 133.81) * mm, "end": v(108, 143.63) * mm});
            skLineSegment(sketch, "E11.0.2.106", {"start": v(53, 133.81) * mm, "end": v(53, 114.19) * mm});
            skLineSegment(sketch, "E11.0.2.107", {"start": v(72, 106.68) * mm, "end": v(57, 115.34) * mm});
            skLineSegment(sketch, "E11.0.2.108", {"start": v(72, 143.63) * mm, "end": v(89, 133.81) * mm});
            skLineSegment(sketch, "E11.0.2.109", {"start": v(109, 145.36) * mm, "end": v(109, 165) * mm});
            skLineSegment(sketch, "E11.0.2.110", {"start": v(161, 114.19) * mm, "end": v(144, 104.37) * mm});
            skLineSegment(sketch, "E11.0.2.111", {"start": v(19, 133.81) * mm, "end": v(36, 143.63) * mm});
            skLineSegment(sketch, "E11.0.2.112", {"start": v(107, 165) * mm, "end": v(107, 145.36) * mm});
            skLineSegment(sketch, "E11.0.2.113", {"start": v(57, 132.66) * mm, "end": v(72, 141.32) * mm});
            skLineSegment(sketch, "E11.0.2.114", {"start": v(1, 145.36) * mm, "end": v(1, 165) * mm});
            skPoint(sketch, "E11.0.2.115", {"position": v(33, 155.18) * mm});
            skLineSegment(sketch, "E11.0.2.116", {"start": v(108, 143.63) * mm, "end": v(125, 133.81) * mm});
            skLineSegment(sketch, "E11.0.2.117", {"start": v(37, 145.36) * mm, "end": v(73, 145.36) * mm, "construction": true});
            skLineSegment(sketch, "E11.0.2.118", {"start": v(54, 135.55) * mm, "end": v(37, 145.36) * mm});
            skLineSegment(sketch, "E11.0.2.119", {"start": v(144, 104.37) * mm, "end": v(127, 114.19) * mm});
            skLineSegment(sketch, "E11.0.2.120", {"start": v(105, 146.52) * mm, "end": v(90, 137.86) * mm});
            skLineSegment(sketch, "E11.0.2.121", {"start": v(72, 141.32) * mm, "end": v(87, 132.66) * mm});
            skLineSegment(sketch, "E11.0.2.122", {"start": v(37, 145.36) * mm, "end": v(37, 165) * mm});
            skLineSegment(sketch, "E11.0.2.123", {"start": v(21, 132.66) * mm, "end": v(36, 141.32) * mm});
            skLineSegment(sketch, "E11.0.2.124", {"start": v(90, 137.86) * mm, "end": v(75, 146.52) * mm});
            skLineSegment(sketch, "E11.0.2.125", {"start": v(105, 146.52) * mm, "end": v(90, 137.86) * mm});
            skLineSegment(sketch, "E11.0.2.126", {"start": v(75, 163.84) * mm, "end": v(90, 172.5) * mm});
            skLineSegment(sketch, "E11.0.2.127", {"start": v(105, 163.84) * mm, "end": v(105, 146.52) * mm});
            skLineSegment(sketch, "E11.0.2.128", {"start": v(90, 172.5) * mm, "end": v(105, 163.84) * mm});
            skLineSegment(sketch, "E11.0.2.129", {"start": v(75, 146.52) * mm, "end": v(75, 163.84) * mm});
            skLineSegment(sketch, "E11.direction1", {"start": v(-17, -9.81) * mm, "end": v(8, -9.81) * mm, "construction": true});
            skLineSegment(sketch, "E11.direction2", {"start": v(-17, -9.81) * mm, "end": v(-17, 52.19) * mm, "construction": true});
            skSolve(sketch);
        }
        {
            var Q0;
            Q0 = qSketchRegion(id + "F0", true);
            extrude(context, id + "F1", {"entities" : qUnion([Q0]), "depth" : 1 * mm, "offsetDistance" : 25 * mm});
        }
    });
